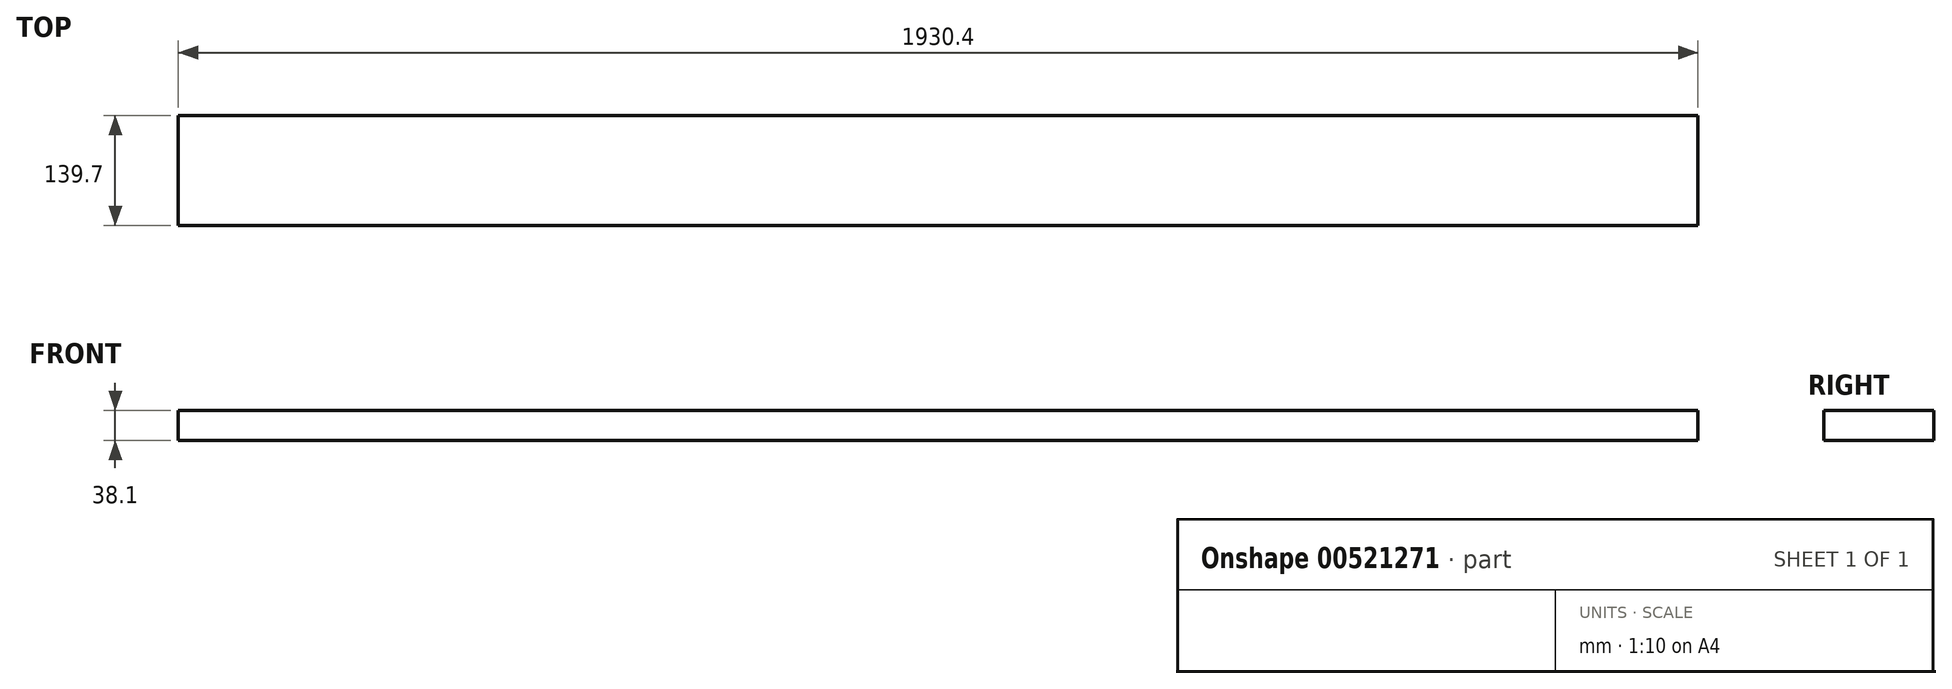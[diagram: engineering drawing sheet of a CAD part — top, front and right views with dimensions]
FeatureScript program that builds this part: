
annotation { "Feature Type Name" : "Feature", "Feature Type Description" : "" }
export const myFeature = defineFeature(function(context is Context, id is Id, definition is map)
    precondition{}
    {
        {
            var Q0;
            Q0=qCreatedBy(makeId("Front.planeOp"),FACE);
            var sketch = newSketch(context, id + "F0", { "sketchPlane" : qUnion([Q0])});
            skLineSegment(sketch, "E0", {"start": v(965.2, 0) * mm, "end": v(-965.2, 0) * mm});
            skLineSegment(sketch, "E1", {"start": v(0, 570.25) * mm, "end": v(0, -656.25) * mm});
            skLineSegment(sketch, "E2", {"start": v(-965.2, 0) * mm, "end": v(-965.2, 38.1) * mm});
            skLineSegment(sketch, "E3", {"start": v(-965.2, 38.1) * mm, "end": v(965.2, 38.1) * mm});
            skLineSegment(sketch, "E4", {"start": v(965.2, 38.1) * mm, "end": v(965.2, 0) * mm});
            skSolve(sketch);
        }
        {
            var Q0;
            {var subQ0=sQuery(id+"F0.wireOp",EDGE,"E2");Q0=makeQuery(id+"F0.imprint","IMPRINT",FACE,{"disambiguationData":[TD([[makeQuery(id+"F0.imprint","IMPRINT",EDGE,{"derivedFrom":subQ0}),-1.0]])]});}
            var Q1;
            {var subQ0=sQuery(id+"F0.wireOp",EDGE,"E4");Q1=makeQuery(id+"F0.imprint","IMPRINT",FACE,{"disambiguationData":[TD([[makeQuery(id+"F0.imprint","IMPRINT",EDGE,{"derivedFrom":subQ0}),-1.0]])]});}
            extrude(context, id + "F1", {"entities" : qUnion([Q0, Q1]), "depth" : 139.7 * mm, "offsetDistance" : 25.4 * mm});
        }
    });
